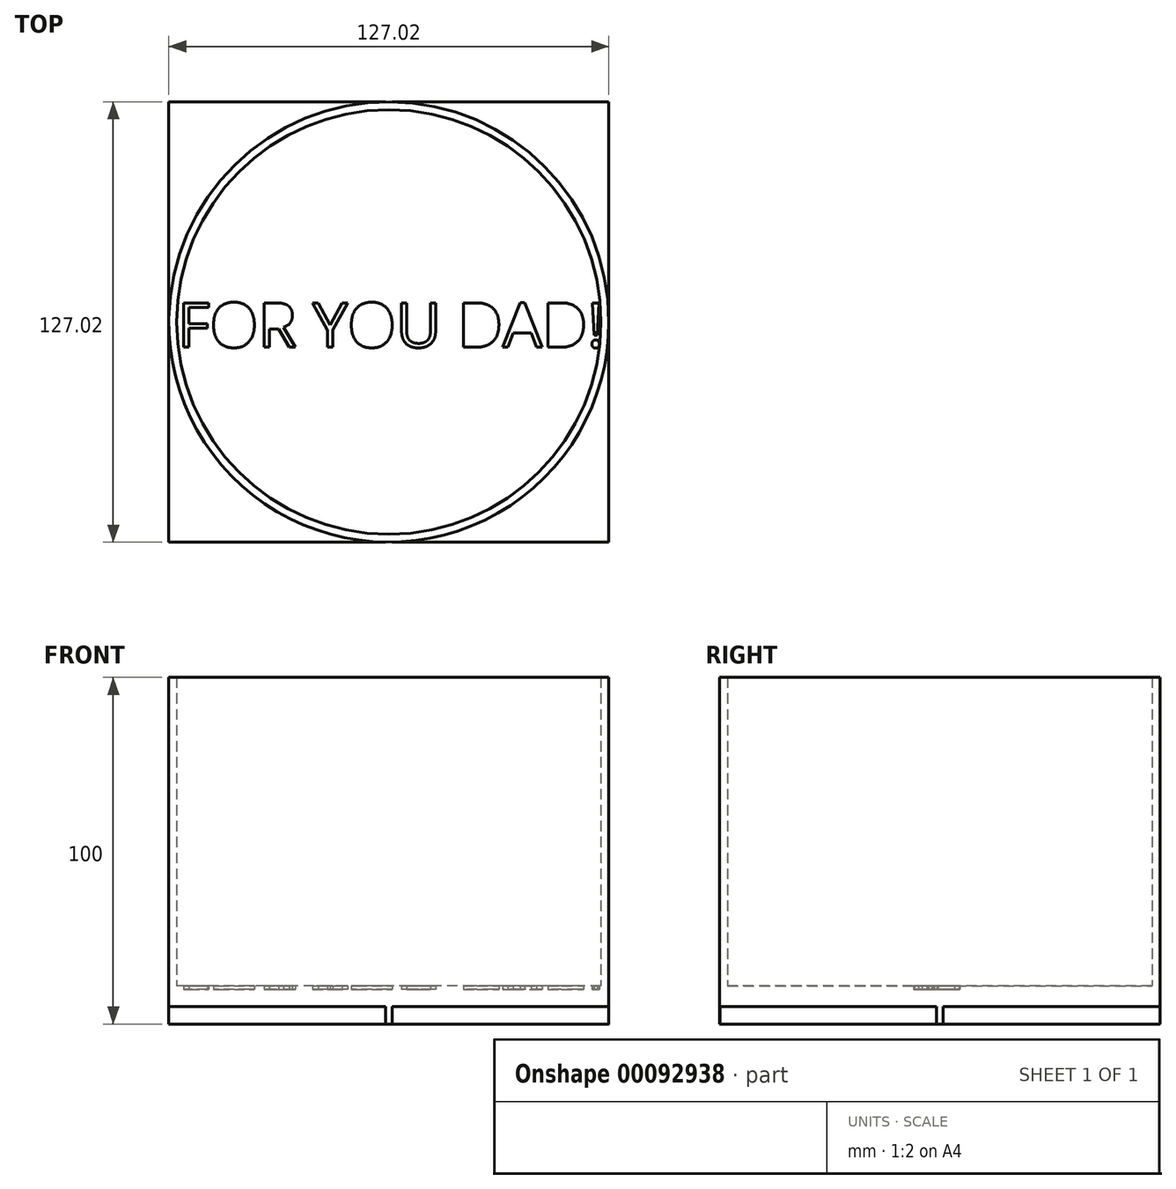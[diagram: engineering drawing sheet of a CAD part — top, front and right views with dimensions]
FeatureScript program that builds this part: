
annotation { "Feature Type Name" : "Feature", "Feature Type Description" : "" }
export const myFeature = defineFeature(function(context is Context, id is Id, definition is map)
    precondition{}
    {
        {
            var Q0;
            Q0=qCreatedBy(makeId("Top.planeOp"),FACE);
            var sketch = newSketch(context, id + "F0", { "sketchPlane" : qUnion([Q0])});
            skCircle(sketch, "E0", {"center": v(0, 0) * mm, "radius": 63.5 * mm});
            skCircle(sketch, "E1", {"center": v(0, 0) * mm, "radius": 61.22 * mm});
            skSolve(sketch);
        }
        {
            var Q0;
            Q0 = qSketchRegion(id + "F0", true);
            extrude(context, id + "F1", {"entities" : qUnion([Q0]), "depth" : 100 * mm});
        }
        {
            var Q0;
            Q0=qCreatedBy(makeId("Top.planeOp"),FACE);
            var sketch = newSketch(context, id + "F2", { "sketchPlane" : qUnion([Q0])});
            skCircle(sketch, "E2.0", {"center": v(0, 0) * mm, "radius": 61.22 * mm});
            skSolve(sketch);
        }
        {
            var Q0;
            Q0 = qSketchRegion(id + "F2", true);
            extrude(context, id + "F3", {"entities" : qUnion([Q0]), "operationType" : NewBodyOperationType.ADD, "depth" : 10 * mm});
        }
        {
            var Q0;
            Q0=qCreatedBy(makeId("Top.planeOp"),FACE);
            var sketch = newSketch(context, id + "F4", { "sketchPlane" : qUnion([Q0])});
            skLineSegment(sketch, "E3.bottom", {"start": v(-63.5, 63.5) * mm, "end": v(63.5, 63.5) * mm});
            skLineSegment(sketch, "E3.top", {"start": v(-63.5, -63.5) * mm, "end": v(63.5, -63.5) * mm});
            skLineSegment(sketch, "E3.left", {"start": v(-63.5, 63.5) * mm, "end": v(-63.5, -63.5) * mm});
            skLineSegment(sketch, "E3.right", {"start": v(63.5, 63.5) * mm, "end": v(63.5, -63.5) * mm});
            skPoint(sketch, "E3.middle", {"position": v(0, 0) * mm});
            skSolve(sketch);
        }
        {
            var Q0;
            Q0 = qSketchRegion(id + "F4", true);
            extrude(context, id + "F5", {"entities" : qUnion([Q0]), "operationType" : NewBodyOperationType.ADD, "depth" : 5 * mm});
        }
        {
            var Q0;
            Q0=qCreatedBy(makeId("Top.planeOp"),FACE);
            var sketch = newSketch(context, id + "F6", { "sketchPlane" : qUnion([Q0])});
            skCircle(sketch, "E4.0.0", {"center": v(0, 0) * mm, "radius": 61.22 * mm});
            skText(sketch, "E5", { "text": "FOR YOU DAD!", "fontName": "OpenSans-Regular.ttf"});
            const initialGuessF6  = {"E5": [-0.06096, -0.00729, 1, 0, 0.01292]};
            skSetInitialGuess(sketch, initialGuessF6);
            skSolve(sketch);
        }
        {
            var Q0;
            Q0 = qSketchRegion(id + "F6", true);
            extrude(context, id + "F7", {"entities" : qUnion([Q0]), "operationType" : NewBodyOperationType.ADD, "depth" : 11 * mm});
        }
    });
